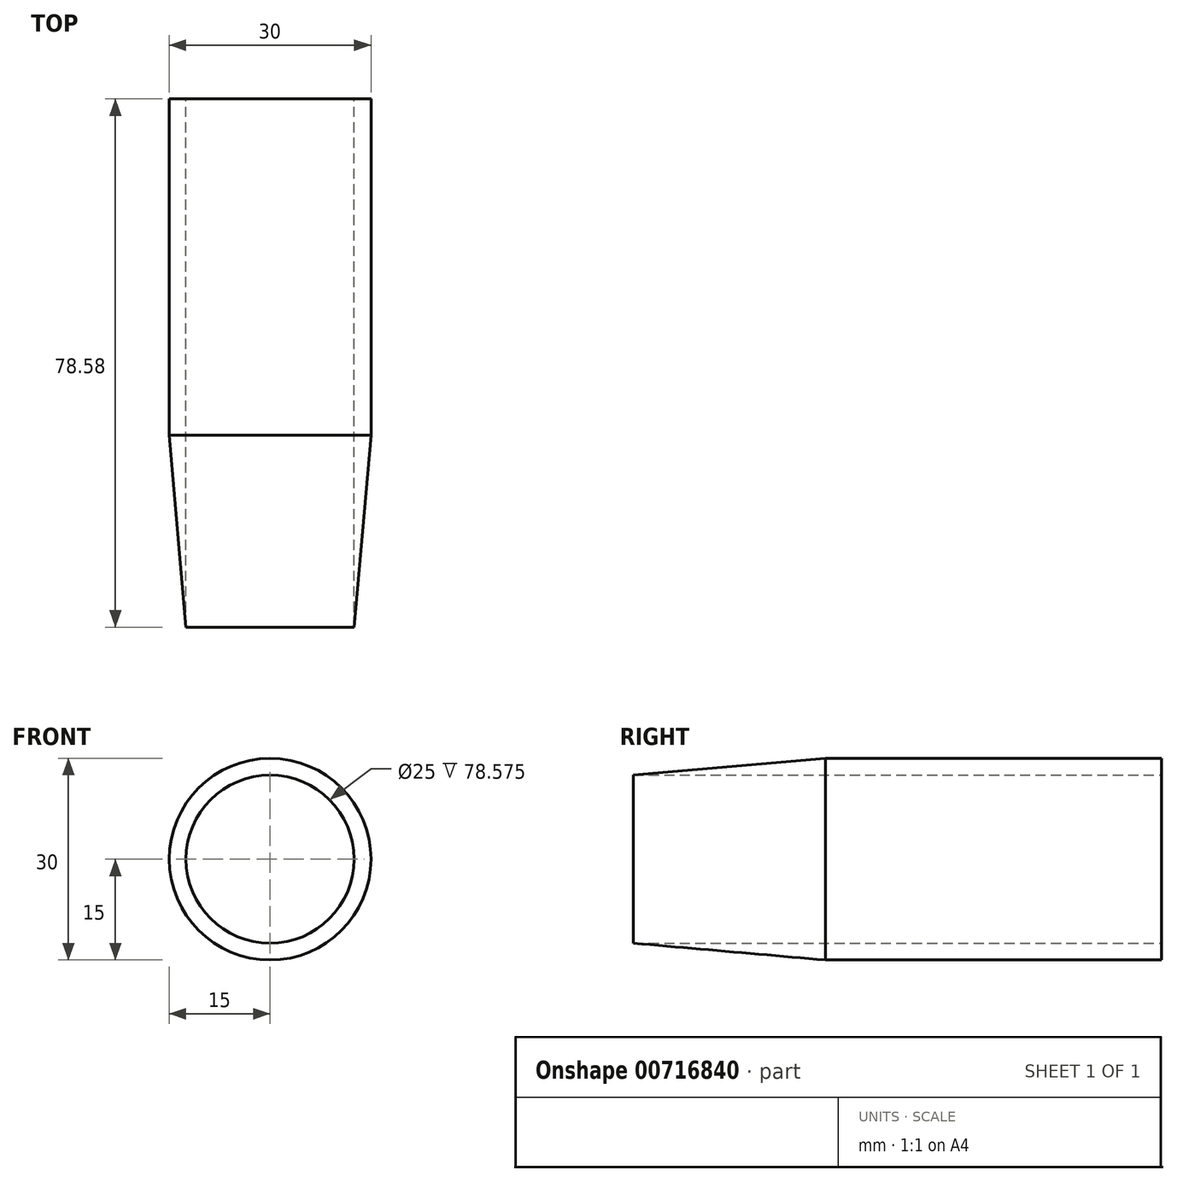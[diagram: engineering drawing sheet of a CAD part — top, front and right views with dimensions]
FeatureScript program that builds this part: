
annotation { "Feature Type Name" : "Feature", "Feature Type Description" : "" }
export const myFeature = defineFeature(function(context is Context, id is Id, definition is map)
    precondition{}
    {
        {
            var Q0;
            Q0=qCreatedBy(makeId("Front.planeOp"),FACE);
            var sketch = newSketch(context, id + "F0", { "sketchPlane" : qUnion([Q0])});
            skCircle(sketch, "E0", {"center": v(0, 0) * mm, "radius": 15 * mm});
            skSolve(sketch);
        }
        {
            var Q0;
            Q0 = qSketchRegion(id + "F0", true);
            extrude(context, id + "F1", {"entities" : qUnion([Q0]), "depth" : 100 * mm, "offsetDistance" : 25 * mm, "hasDraft" : true, "draftAngle" : 5 * degree, "draftPullDirection" : true, "hasSecondDirection" : true, "secondDirectionOppositeDirection" : true, "secondDirectionDepth" : 50 * mm});
        }
        {
            var Q0;
            Q0=makeQuery(id+"F1.opExtrude","CAP_FACE",FACE,{"disambiguationData":[OSD([sQuery(id+"F0.wireOp",EDGE,"E0")])],"isStart":true});
            var Q1;
            Q1=makeQuery(id+"F1.*.split.splitOp","SPLIT",FACE,{"derivedFrom":makeQuery(id+"F1.opExtrude","SWEPT_FACE",FACE,{"disambiguationData":[OSD([sQuery(id+"F0.wireOp",EDGE,"E0")])]})});
            var Q2;
            Q2=makeQuery(id+"F1.opExtrude","CAP_FACE",FACE,{"disambiguationData":[OSD([sQuery(id+"F0.wireOp",EDGE,"E0")])],"isStart":false});
            shell(context, id + "F2", {"entities" : qUnion([Q0, Q1, Q2]), "thickness" : 2.5 * mm});
        }
    });
